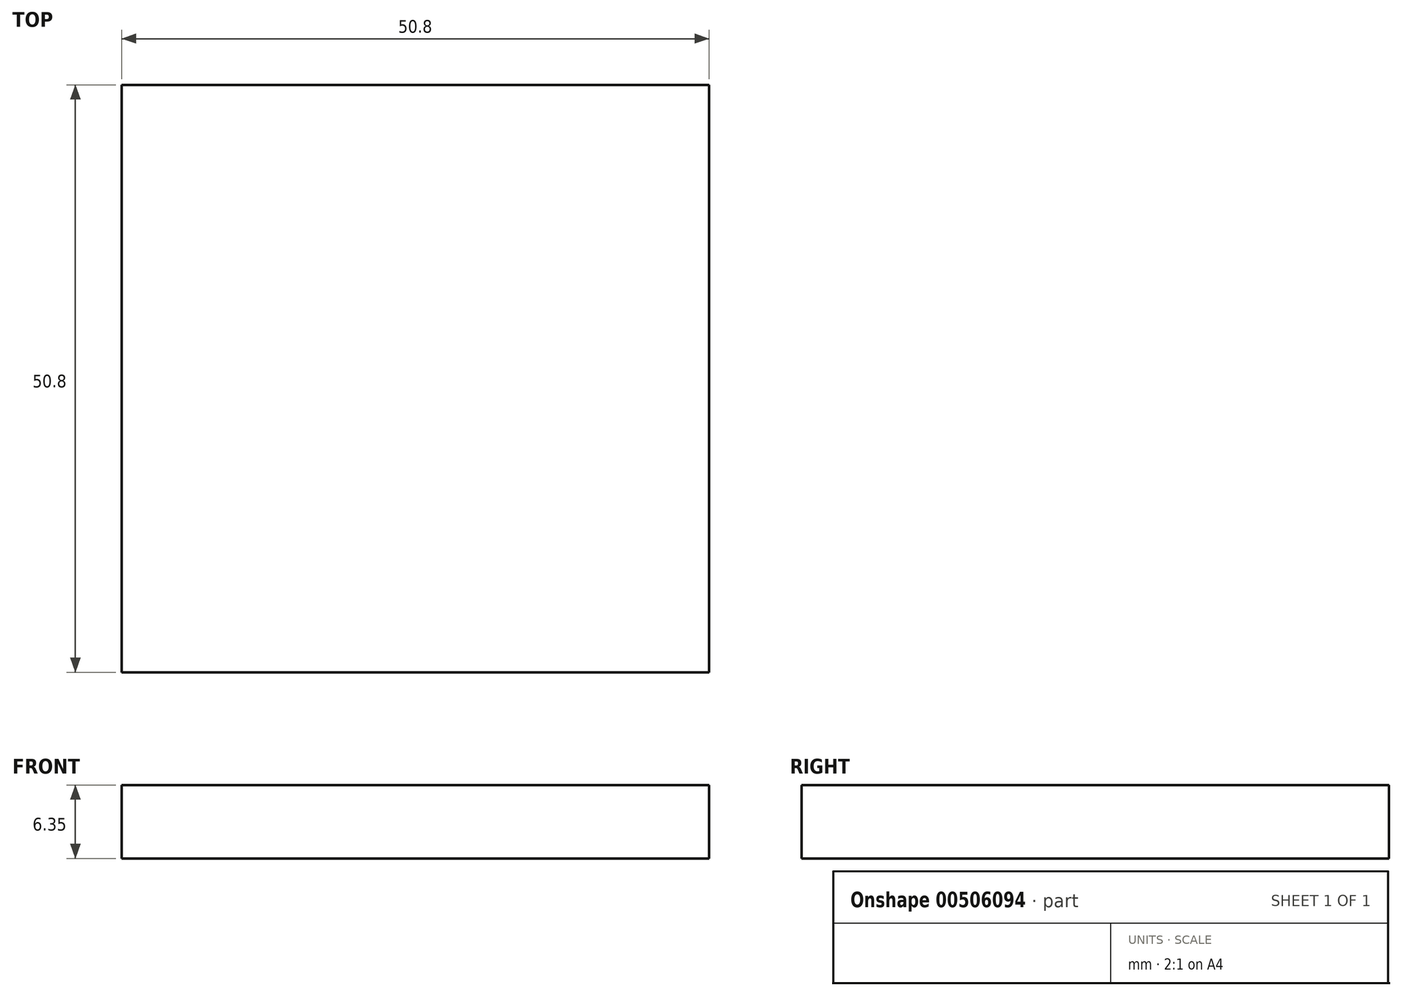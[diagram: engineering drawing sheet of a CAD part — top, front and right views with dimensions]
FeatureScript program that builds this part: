
annotation { "Feature Type Name" : "Feature", "Feature Type Description" : "" }
export const myFeature = defineFeature(function(context is Context, id is Id, definition is map)
    precondition{}
    {
        {
            var Q0;
            Q0=qCreatedBy(makeId("Top.planeOp"),FACE);
            var sketch = newSketch(context, id + "F0", { "sketchPlane" : qUnion([Q0])});
            skLineSegment(sketch, "E0.bottom", {"start": v(0, 0) * mm, "end": v(50.8, 0) * mm});
            skLineSegment(sketch, "E0.top", {"start": v(0, 50.8) * mm, "end": v(50.8, 50.8) * mm});
            skLineSegment(sketch, "E0.left", {"start": v(0, 0) * mm, "end": v(0, 50.8) * mm});
            skLineSegment(sketch, "E0.right", {"start": v(50.8, 0) * mm, "end": v(50.8, 50.8) * mm});
            skSolve(sketch);
        }
        {
            var Q0;
            Q0 = qSketchRegion(id + "F0", true);
            extrude(context, id + "F1", {"entities" : qUnion([Q0]), "oppositeDirection" : true, "depth" : 6.35 * mm});
        }
    });
